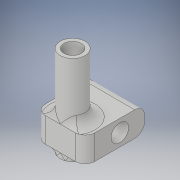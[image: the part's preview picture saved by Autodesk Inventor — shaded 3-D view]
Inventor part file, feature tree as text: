
AUTODESK INVENTOR PART (.ipt)
format: ipt  version: 2019.4 (Build 234330000, 330)  size: 221,696 bytes
history: native  units: mm
features: extrude x4, sketch x4, fillet x2, plane x1
ambient origin geometry x8: Origin, YZ Plane, XZ Plane, XY Plane, X Axis, Y Axis, Z Axis, Center Point
bodies: Solid1 (feature_tree)
feature tree (11):
  extrude  "Extrusion1"  Depth=5.0mm
  plane  "Work Plane1"
  extrude  "Extrusion2"  Depth=2.5mm
  extrude  "Extrusion3"  TaperAngle=90.0deg  [1 undecoded]
  fillet  "Fillet1"  Radius=10.0mm
  fillet  "Fillet2"  Radius=5.0mm
  extrude  "Extrusion4"  Depth=2.0mm
  sketch  "Sketch1"  dims[d0=3.5mm d1=5.0mm]
  sketch  "Sketch3"  dims[d2=18.0mm d3=0.0mm d7=2.5mm]
  sketch  "Sketch4"  dims[d8=14.45mm d9=90.0deg d10=10.0mm d11=5.0mm]
  sketch  "Sketch5"  dims[d12=12.0mm d13=0.0mm d14=5.0mm d15=3.5mm d16=12.0mm d17=0.0mm d18=2.0mm d19=2.0mm d20=3.5mm d21=20.0mm d22=0.0mm]
note: 1 required parameter value undecoded (feature->parameter linkage not recoverable at this tier; creation-order binding heuristic only, values carry confidence <= 0.55)
